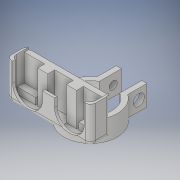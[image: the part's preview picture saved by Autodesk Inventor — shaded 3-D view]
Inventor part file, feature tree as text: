
AUTODESK INVENTOR PART (.ipt)
format: ipt  version: 2018 (Build 220112000, 112)  size: 324,096 bytes
history: native  units: in
note: dims shown in document units (in); Inventor stores cm internally (conversion verified against a paired STEP export)
features: extrude x8, sketch x8, fillet x4, reference x3, other x2, projected_geometry x1
ambient origin geometry x8: Origin, YZ Plane, XZ Plane, XY Plane, X Axis, Y Axis, Z Axis, Center Point
bodies: Solid1 (feature_tree)
feature tree (26):
  extrude  "Extrusion1"  Depth=0.125in
  extrude  "Extrusion2"  Depth=0.125in
  extrude  "Extrusion3"  Depth=0.125in
  extrude  "Extrusion4"  Depth=0.25in
  extrude  "Extrusion5"  Depth=0.194in
  extrude  "Extrusion7"  Depth=0.04in
  extrude  "Extrusion8"  Depth=0.8125in TaperAngle=0.0deg
  extrude  "Extrusion9"  Depth=0.125in
  fillet  "Fillet1"  Radius=0.05in
  fillet  "Fillet2"  Radius=0.05in
  fillet  "Fillet3"  Radius=0.05in
  fillet  "Fillet4"  Radius=0.05in
  sketch  "Sketch1"  dims[d0=1.05in d1=0.125in]
  sketch  "Sketch2"  dims[d2=0.125in d3=0.375in]
  sketch  "Sketch3"  dims[d4=1.0in d5=0.125in]
  sketch  "Sketch4"  dims[d6=0.5in d7=0.0in d8=0.25in]
  sketch  "Sketch5"  dims[d9=0.2in d10=0.194in]
  sketch  "Sketch7"  dims[d11=1.0in d12=0.0in d13=0.04in]
  projected_geometry  "Projected Loop3"
  sketch  "Sketch8"  dims[d14=1.0in d15=0.0in d18=0.8125in d19=0.0in]
  sketch  "Sketch9"  dims[d20=1.95in d21=0.975in d22=0.05in d23=0.05in d24=0.05in d25=0.05in d26=0.445in d27=0.0in d28=0.9125in d29=0.8in d30=0.05in d31=0.05in d35=0.17in d36=0.0in d37=0.25in d38=0.25in d39=0.5in d40=0.5in d41=0.17in d42=0.0in d43=0.05in d44=0.05in d45=0.0625in d46=0.0in d47=0.05in d48=0.125in d49=0.125in d50=0.25in d51=0.125in]
  reference  "Reference1"
  reference  "Reference2"
  reference  "Reference3"
  other  "Assembly1"
  other  "Ultrasonic_sensor:1"
